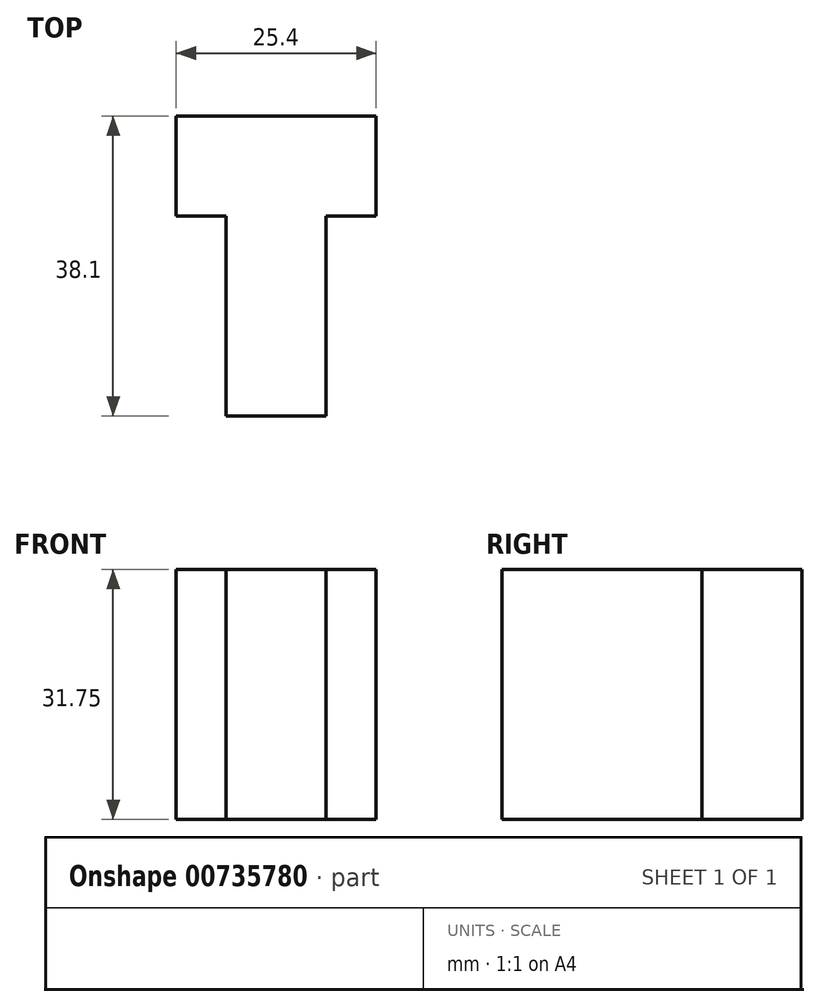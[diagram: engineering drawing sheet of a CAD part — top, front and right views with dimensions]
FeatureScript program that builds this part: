
annotation { "Feature Type Name" : "Feature", "Feature Type Description" : "" }
export const myFeature = defineFeature(function(context is Context, id is Id, definition is map)
    precondition{}
    {
        {
            var Q0;
            Q0=qCreatedBy(makeId("Top.planeOp"),FACE);
            var sketch = newSketch(context, id + "F0", { "sketchPlane" : qUnion([Q0])});
            skLineSegment(sketch, "E0", {"start": v(0, 0) * mm, "end": v(12.7, 0) * mm});
            skLineSegment(sketch, "E1", {"start": v(12.7, 0) * mm, "end": v(12.7, 25.4) * mm});
            skLineSegment(sketch, "E2", {"start": v(12.7, 25.4) * mm, "end": v(19.05, 25.4) * mm});
            skLineSegment(sketch, "E3", {"start": v(19.05, 25.4) * mm, "end": v(19.05, 38.1) * mm});
            skLineSegment(sketch, "E4", {"start": v(19.05, 38.1) * mm, "end": v(-6.35, 38.1) * mm});
            skLineSegment(sketch, "E5", {"start": v(-6.35, 38.1) * mm, "end": v(-6.35, 25.4) * mm});
            skLineSegment(sketch, "E6", {"start": v(-6.35, 25.4) * mm, "end": v(0, 25.4) * mm});
            skLineSegment(sketch, "E7", {"start": v(0, 25.4) * mm, "end": v(0, 0) * mm});
            skSolve(sketch);
        }
        {
            var Q0;
            Q0=makeQuery(id+"F0.imprint","IMPRINT",FACE,{"disambiguationData":[TD([[makeQuery(id+"F0.imprint","IMPRINT",EDGE,{"derivedFrom":sQuery(id+"F0.wireOp",EDGE,"E0")}),1.0]])]});
            extrude(context, id + "F1", {"entities" : qUnion([Q0]), "depth" : 31.75 * mm, "offsetDistance" : 25.4 * mm});
        }
    });
